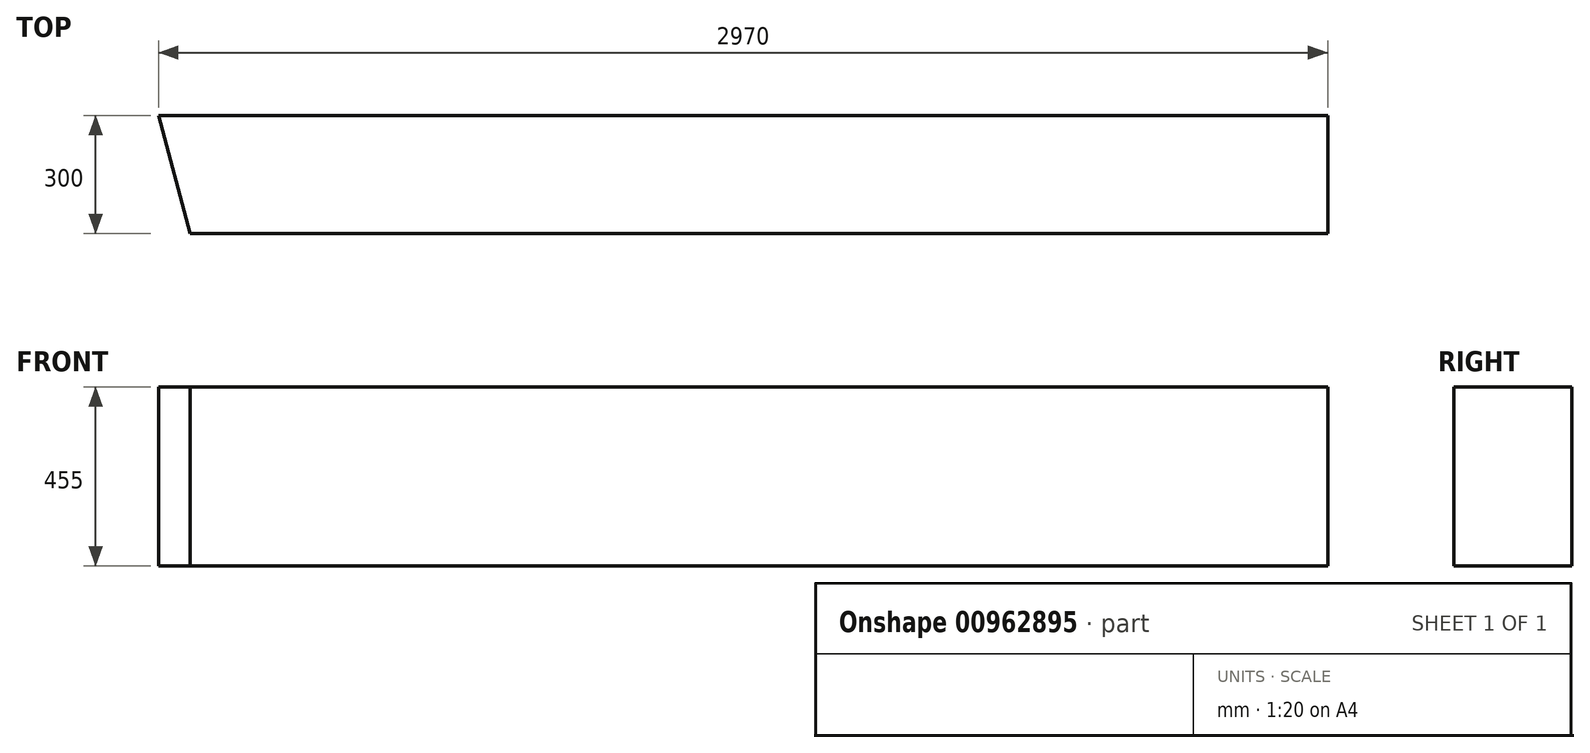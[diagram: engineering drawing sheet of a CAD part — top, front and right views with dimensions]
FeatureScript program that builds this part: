
annotation { "Feature Type Name" : "Feature", "Feature Type Description" : "" }
export const myFeature = defineFeature(function(context is Context, id is Id, definition is map)
    precondition{}
    {
        {
            var Q0;
            Q0=qCreatedBy(makeId("Top.planeOp"),FACE);
            var sketch = newSketch(context, id + "F0", { "sketchPlane" : qUnion([Q0])});
            skLineSegment(sketch, "E0", {"start": v(-1591.6, 357) * mm, "end": v(1378.4, 357) * mm});
            skLineSegment(sketch, "E1", {"start": v(1378.4, 357) * mm, "end": v(1378.4, 57) * mm});
            skLineSegment(sketch, "E2", {"start": v(1378.4, 57) * mm, "end": v(-1511.22, 57) * mm});
            skLineSegment(sketch, "E3", {"start": v(-1511.22, 57) * mm, "end": v(-1591.6, 357) * mm});
            skSolve(sketch);
        }
        {
            var Q0;
            Q0 = qSketchRegion(id + "F0", true);
            extrude(context, id + "F1", {"entities" : qUnion([Q0]), "depth" : 455 * mm, "offsetDistance" : 25 * mm});
        }
    });
